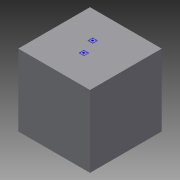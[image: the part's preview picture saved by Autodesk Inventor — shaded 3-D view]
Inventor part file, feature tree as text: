
AUTODESK INVENTOR PART (.ipt)
format: ipt  version: 2014 (Build 180170000, 170)  size: 248,320 bytes
history: native  units: mm
features: other x50, sketch x3, extrude x1
ambient origin geometry x8: Origin, YZ Plane, XZ Plane, XY Plane, X Axis, Y Axis, Z Axis, Center Point
bodies: 实体1 (feature_tree)
feature tree (54):
  extrude  "拉伸1"  TaperAngle=0.0deg  [1 undecoded]
  other  "UCS1"
  other  "UCS2"
  other  "UCS3"
  other  "UCS4"
  other  "UCS5"
  other  "UCS6"
  other  "Footprint7"
  other  "Footprint2"
  sketch  "草图1"  dims[d0=1000.0mm d1=0.0mm]
  other  "UCS1: YZ 平面"
  other  "UCS1: XZ 平面"
  other  "UCS1: XY 平面"
  other  "UCS1: X 轴"
  other  "UCS1: Y 轴"
  other  "UCS1: Z 轴"
  other  "UCS1: 原点"
  other  "UCS2: YZ 平面"
  other  "UCS2: XZ 平面"
  other  "UCS2: XY 平面"
  other  "UCS2: X 轴"
  other  "UCS2: Y 轴"
  other  "UCS2: Z 轴"
  other  "UCS2: 原点"
  other  "UCS3: YZ 平面"
  other  "UCS3: XZ 平面"
  other  "UCS3: XY 平面"
  other  "UCS3: X 轴"
  other  "UCS3: Y 轴"
  other  "UCS3: Z 轴"
  other  "UCS3: 原点"
  other  "UCS4: YZ 平面"
  other  "UCS4: XZ 平面"
  other  "UCS4: XY 平面"
  other  "UCS4: X 轴"
  other  "UCS4: Y 轴"
  other  "UCS4: Z 轴"
  other  "UCS4: 原点"
  other  "UCS5: YZ 平面"
  other  "UCS5: XZ 平面"
  other  "UCS5: XY 平面"
  other  "UCS5: X 轴"
  other  "UCS5: Y 轴"
  other  "UCS5: Z 轴"
  other  "UCS5: 原点"
  other  "UCS6: YZ 平面"
  other  "UCS6: XZ 平面"
  other  "UCS6: XY 平面"
  other  "UCS6: X 轴"
  other  "UCS6: Y 轴"
  other  "UCS6: Z 轴"
  other  "UCS6: 原点"
  sketch  "草图15"  dims[d2=0.0mm d3=0.0mm d4=0.0mm d5=0.0mm d6=0.0mm d7=0.0mm]
  sketch  "草图17"  dims[d8=0.0mm d9=0.0mm d10=0.0mm d11=0.0mm d12=0.0mm d13=0.0mm d14=0.0mm d15=0.0mm d16=0.0mm d17=0.0mm d18=0.0mm d19=0.0mm d20=0.0mm d21=0.0mm d22=0.0mm d23=0.0mm d24=0.0mm d25=0.0mm d26=0.0mm d27=0.0mm d28=0.0mm d29=0.0mm d30=0.0mm d31=0.0mm d32=0.0mm d33=0.0mm d34=0.0mm d35=0.0mm d36=0.0mm d37=0.0mm d38=0.0mm d44=0.0mm d48=0.0mm d54=0.0mm d60=0.0mm d66=0.0mm d72=0.0mm d73=0.0mm d84=0.0mm]
note: 1 required parameter value undecoded (feature->parameter linkage not recoverable at this tier; creation-order binding heuristic only, values carry confidence <= 0.55)
